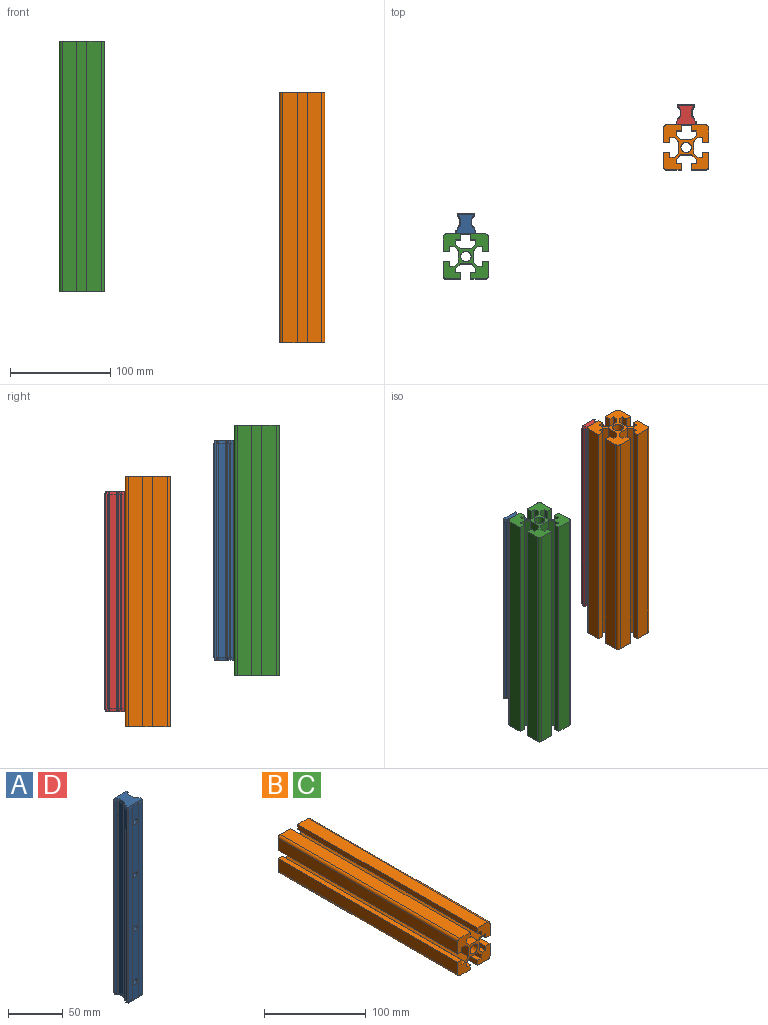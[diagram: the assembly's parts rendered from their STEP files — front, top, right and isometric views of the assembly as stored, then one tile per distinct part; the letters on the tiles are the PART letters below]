
ASSEMBLY  parts=4 mates=2
PART A: 102 faces, bbox 20.1x20.6x220.1 mm
  f0: plane 3.02x1.64mm, normal (0.49,0.85,0.17), area 4mm2, adj f1,f29,f51,f77
  f1: plane 7.51x3mm, normal (0.98,0,0.17), area 21.9mm2, adj f0,f2,f29,f78
  f2: plane 3.04x1.66mm, normal (0.49,-0.85,0.17), area 4mm2, adj f1,f29,f52,f79
  f3: plane 3.07x2.45mm, normal (0.98,0,0.17), area 6.2mm2, adj f29,f50,f51,f75
  f4: plane 3.07x1.9mm, normal (-0.98,0,0.17), area 4.6mm2, adj f29,f35,f36,f57
  f5: plane 3x2.38mm, normal (0.98,0,-0.17), area 6.2mm2, adj f75,f85,f98,f99
  f6: cylinder r=3mm len=12.9mm, axis (0,-1,0), area 243.2mm2, adj f27,f69
  f7: cylinder r=3mm len=12.9mm, axis (0,-1,0), area 243.2mm2, adj f26,f69
  f8: plane 9.4x9.4mm, normal (0,-1,0), area 69.4mm2, adj f19
  f9: plane 3x1.83mm, normal (-0.98,0,-0.17), area 4.6mm2, adj f57,f84,f85,f93
  f10: cone r=2.57mm half-angle=10deg, axis (0,0,-1), area 8mm2, adj f11,f62,f85,f94
  f11: plane 3.04x1.66mm, normal (-0.49,0.85,-0.17), area 4mm2, adj f10,f12,f61,f85
  f12: plane 7.51x3mm, normal (-0.98,0,-0.17), area 21.9mm2, adj f11,f13,f60,f85
  f13: plane 3.02x1.64mm, normal (-0.49,-0.85,-0.17), area 4mm2, adj f12,f59,f85,f93
  f14: plane 9.4x9.4mm, normal (0,-1,0), area 69.4mm2, adj f17
  f15: plane 9.4x9.4mm, normal (0,-1,0), area 69.4mm2, adj f18
  f16: plane 9.4x9.4mm, normal (0,-1,0), area 69.4mm2, adj f20
  f17: cylinder r=4.7mm len=9.4mm, axis (0,-1,0), area 199.3mm2, adj f14,f25
  f18: cylinder r=4.7mm len=9.4mm, axis (0,-1,0), area 199.3mm2, adj f15,f26
  f19: cylinder r=4.7mm len=9.4mm, axis (0,-1,0), area 199.3mm2, adj f8,f27
  f20: cylinder r=4.7mm len=9.4mm, axis (0,-1,0), area 199.3mm2, adj f16,f28
  f21: plane 9.4x9.4mm, normal (0,1,0), area 69.4mm2, adj f31
  f22: plane 9.4x9.4mm, normal (0,1,0), area 69.4mm2, adj f32
  f23: plane 9.4x9.4mm, normal (0,1,0), area 69.4mm2, adj f33
  f24: plane 9.4x9.4mm, normal (0,1,0), area 69.4mm2, adj f34
  f25: plane 9.4x9.4mm, normal (0,1,0), area 41.1mm2, adj f17,f45
  f26: plane 9.4x9.4mm, normal (0,1,0), area 41.1mm2, adj f7,f18
  f27: plane 9.4x9.4mm, normal (0,1,0), area 41.1mm2, adj f6,f19
  f28: plane 9.4x9.4mm, normal (0,1,0), area 41.1mm2, adj f20,f46
  f29: plane 19.49x18.94mm, normal (0,0,1), area 271.6mm2, adj f0,f1,f2,f3,f4,f30,f35,f36
  f30: plane 16.61x3mm, normal (0,0.98,0.17), area 49.9mm2, adj f29,f35,f54,f55
  f31: cylinder r=4.7mm len=9.4mm, axis (0,-1,0), area 3mm2, adj f21,f55
  f32: cylinder r=4.7mm len=9.4mm, axis (0,-1,0), area 3mm2, adj f22,f55
  f33: cylinder r=4.7mm len=9.4mm, axis (0,-1,0), area 3mm2, adj f23,f55
  f34: cylinder r=4.7mm len=9.4mm, axis (0,-1,0), area 3mm2, adj f24,f55
  f35: plane 3x0.71mm, normal (-0.7,0.7,0.17), area 1.5mm2, adj f4,f29,f30,f56
  f36: cone r=2.57mm half-angle=10deg, axis (0,0,1), area 8mm2, adj f4,f29,f37,f58
  f37: plane 3.02x1.64mm, normal (-0.49,-0.85,0.17), area 4mm2, adj f29,f36,f38,f59
  f38: plane 7.51x3mm, normal (-0.98,0,0.17), area 21.9mm2, adj f29,f37,f39,f60
  f39: plane 3.04x1.66mm, normal (-0.49,0.85,0.17), area 4mm2, adj f29,f38,f40,f61
  f40: cone r=2.57mm half-angle=10deg, axis (0,0,1), area 8mm2, adj f29,f39,f41,f62
  f41: plane 3x2.38mm, normal (-0.98,0,0.17), area 6.2mm2, adj f29,f40,f42,f63
  f42: plane 3x1.73mm, normal (-0.49,0.85,0.17), area 4.2mm2, adj f29,f41,f43,f64
  f43: plane 3x2.61mm, normal (-0.98,0,0.17), area 7.1mm2, adj f29,f42,f44,f65
  f44: plane 3x1.42mm, normal (-0.7,-0.7,0.17), area 4.5mm2, adj f29,f43,f47,f66
  f45: cylinder r=3mm len=12.9mm, axis (0,-1,0), area 243.2mm2, adj f25,f69
  f46: cylinder r=3mm len=12.9mm, axis (0,-1,0), area 243.2mm2, adj f28,f69
  f47: plane 17.6x3mm, normal (0,-0.98,0.17), area 39.6mm2, adj f29,f44,f48,f67,f68,f69,f70,f71
  f48: plane 3x1.42mm, normal (0.7,-0.7,0.17), area 4.5mm2, adj f29,f47,f49,f72
  f49: plane 3x2.61mm, normal (0.98,0,0.17), area 7.1mm2, adj f29,f48,f50,f73
  f50: plane 3x1.73mm, normal (0.49,0.85,0.17), area 4.2mm2, adj f3,f29,f49,f74
  f51: cone r=2.57mm half-angle=10deg, axis (0,0,1), area 8mm2, adj f0,f3,f29,f76
  f52: cone r=2.57mm half-angle=10deg, axis (0,0,1), area 8mm2, adj f2,f29,f53,f80
  f53: plane 3x1.83mm, normal (0.98,0,0.17), area 4.6mm2, adj f29,f52,f54,f81
  f54: plane 3x0.71mm, normal (0.7,0.7,0.17), area 1.5mm2, adj f29,f30,f53,f82
  f55: plane 214x16.61mm, normal (0,1,0), area 3277mm2, adj f30,f31,f32,f33,f34,f56,f82,f83
  f56: plane 214x0.5mm, normal (-0.71,0.71,0), area 149.8mm2, adj f35,f55,f57,f84
  f57: plane 214x1.83mm, normal (-1,0,0), area 391.7mm2, adj f4,f9,f56,f58
  f58: cylinder r=2.31mm len=214mm, axis (0,0,-1), area 568.4mm2, adj f36,f57,f59,f93
  f59: plane 214x1.09mm, normal (-0.5,-0.87,0), area 269.8mm2, adj f13,f37,f58,f60
  f60: plane 214x6.9mm, normal (-1,0,0), area 1476.6mm2, adj f12,f38,f59,f61
  f61: plane 214x1.09mm, normal (-0.5,0.87,0), area 269.8mm2, adj f11,f39,f60,f62
  f62: cylinder r=2.31mm len=214mm, axis (0,0,-1), area 568.4mm2, adj f10,f40,f61,f63
  f63: plane 214x2.08mm, normal (-1,0,0), area 444.1mm2, adj f41,f62,f64,f94
  f64: plane 214x1.2mm, normal (-0.5,0.87,0), area 296.5mm2, adj f42,f63,f65,f92
  f65: plane 214x2.61mm, normal (-1,0,0), area 557.9mm2, adj f43,f64,f66,f91
  f66: plane 214x1.2mm, normal (-0.71,-0.71,0), area 363.2mm2, adj f44,f65,f67,f90
  f67: plane 214x4.8mm, normal (0,-1,0), area 1027.2mm2, adj f47,f66,f68,f97
  f68: plane 217.4x0.3mm, normal (0.71,-0.71,0), area 91.5mm2, adj f47,f67,f69,f97
  f69: plane 217.4x7.4mm, normal (0,-1,0), area 1495.7mm2, adj f6,f7,f45,f46,f47,f68,f70,f97
  f70: plane 217.4x0.3mm, normal (-0.71,-0.71,0), area 91.5mm2, adj f47,f69,f71,f97
  f71: plane 214x4.8mm, normal (0,-1,0), area 1027.2mm2, adj f47,f70,f72,f97
  f72: plane 214x1.2mm, normal (0.71,-0.71,0), area 363.2mm2, adj f48,f71,f73,f95
  f73: plane 214x2.61mm, normal (1,0,0), area 557.9mm2, adj f49,f72,f74,f96
  f74: plane 214x1.2mm, normal (0.5,0.87,0), area 296.5mm2, adj f50,f73,f75,f98
  f75: plane 214x2.08mm, normal (1,0,0), area 444.1mm2, adj f3,f5,f74,f76
  f76: cylinder r=2.31mm len=214mm, axis (0,0,-1), area 568.4mm2, adj f51,f75,f77,f99
  f77: plane 214x1.09mm, normal (0.5,0.87,0), area 269.8mm2, adj f0,f76,f78,f89
  f78: plane 214x6.9mm, normal (1,0,0), area 1476.6mm2, adj f1,f77,f79,f88
  f79: plane 214x1.09mm, normal (0.5,-0.87,0), area 269.8mm2, adj f2,f78,f80,f87
  f80: cylinder r=2.31mm len=214mm, axis (0,0,-1), area 568.4mm2, adj f52,f79,f81,f100
  f81: plane 214x1.83mm, normal (1,0,0), area 391.7mm2, adj f53,f80,f82,f101
  f82: plane 214x0.5mm, normal (0.71,0.71,0), area 149.8mm2, adj f54,f55,f81,f86
  f83: plane 16.61x3mm, normal (0,0.98,-0.17), area 49.9mm2, adj f55,f84,f85,f86
  f84: plane 3x0.71mm, normal (-0.7,0.7,-0.17), area 1.5mm2, adj f9,f56,f83,f85
  f85: plane 19.49x18.94mm, normal (0,0,-1), area 271.6mm2, adj f5,f9,f10,f11,f12,f13,f83,f84
  f86: plane 3x0.71mm, normal (0.7,0.7,-0.17), area 1.5mm2, adj f82,f83,f85,f101
  f87: plane 3.04x1.66mm, normal (0.49,-0.85,-0.17), area 4mm2, adj f79,f85,f88,f100
  f88: plane 7.51x3mm, normal (0.98,0,-0.17), area 21.9mm2, adj f78,f85,f87,f89
  f89: plane 3.02x1.64mm, normal (0.49,0.85,-0.17), area 4mm2, adj f77,f85,f88,f99
  f90: plane 3x1.42mm, normal (-0.7,-0.7,-0.17), area 4.5mm2, adj f66,f85,f91,f97
  f91: plane 3x2.61mm, normal (-0.98,0,-0.17), area 7.1mm2, adj f65,f85,f90,f92
  f92: plane 3x1.73mm, normal (-0.49,0.85,-0.17), area 4.2mm2, adj f64,f85,f91,f94
  f93: cone r=2.57mm half-angle=10deg, axis (0,0,-1), area 8mm2, adj f9,f13,f58,f85
  f94: plane 3x2.38mm, normal (-0.98,0,-0.17), area 6.2mm2, adj f10,f63,f85,f92
  f95: plane 3x1.42mm, normal (0.7,-0.7,-0.17), area 4.5mm2, adj f72,f85,f96,f97
  f96: plane 3x2.61mm, normal (0.98,0,-0.17), area 7.1mm2, adj f73,f85,f95,f98
  f97: plane 17.6x3mm, normal (0,-0.98,-0.17), area 39.6mm2, adj f67,f68,f69,f70,f71,f85,f90,f95
  f98: plane 3x1.73mm, normal (0.49,0.85,-0.17), area 4.2mm2, adj f5,f74,f85,f96
  f99: cone r=2.57mm half-angle=10deg, axis (0,0,-1), area 8mm2, adj f5,f76,f85,f89
  f100: cone r=2.57mm half-angle=10deg, axis (0,0,-1), area 8mm2, adj f80,f85,f87,f101
  f101: plane 3x1.83mm, normal (0.98,0,-0.17), area 4.6mm2, adj f81,f85,f86,f100
PART B: 51 faces, bbox 45x250x45 mm
  f0: plane 250x6mm, normal (-1,0,0), area 1500mm2, adj f1,f48,f49,f50
  f1: plane 250x14.5mm, normal (0,0,-1), area 3625mm2, adj f0,f2,f49,f50
  f2: cylinder r=3mm len=250mm, axis (0,-1,0), area 1178.1mm2, adj f1,f3,f49,f50
  f3: plane 250x14.5mm, normal (1,0,0), area 3625mm2, adj f2,f4,f49,f50
  f4: plane 250x6mm, normal (0,0,1), area 1500mm2, adj f3,f5,f49,f50
  f5: plane 250x5mm, normal (-1,0,0), area 1250mm2, adj f4,f6,f49,f50
  f6: plane 250x4.73mm, normal (0,0,1), area 1183.1mm2, adj f5,f7,f49,f50
  f7: plane 250x4.27mm, normal (0.71,0,0.71), area 1508.9mm2, adj f6,f8,f49,f50
  f8: plane 250x11.46mm, normal (1,0,0), area 2866.1mm2, adj f7,f9,f49,f50
  f9: plane 250x4.27mm, normal (0.71,0,-0.71), area 1508.9mm2, adj f8,f10,f49,f50
  f10: plane 250x4.73mm, normal (0,0,-1), area 1183.1mm2, adj f9,f11,f49,f50
  f11: plane 250x5mm, normal (-1,0,0), area 1250mm2, adj f10,f12,f49,f50
  f12: plane 250x6mm, normal (0,0,-1), area 1500mm2, adj f11,f13,f49,f50
  f13: plane 250x14.5mm, normal (1,0,0), area 3625mm2, adj f12,f14,f49,f50
  f14: cylinder r=3mm len=250mm, axis (0,-1,0), area 1178.1mm2, adj f13,f15,f49,f50
  f15: plane 250x14.5mm, normal (0,0,1), area 3625mm2, adj f14,f16,f49,f50
  f16: plane 250x6mm, normal (-1,0,0), area 1500mm2, adj f15,f17,f49,f50
  f17: plane 250x5mm, normal (0,0,-1), area 1250mm2, adj f16,f18,f49,f50
  f18: plane 250x4.73mm, normal (-1,0,0), area 1183.1mm2, adj f17,f19,f49,f50
  f19: plane 250x4.27mm, normal (-0.71,0,0.71), area 1508.9mm2, adj f18,f20,f49,f50
  f20: plane 250x11.46mm, normal (0,0,1), area 2866.1mm2, adj f19,f21,f49,f50
  f21: plane 250x4.27mm, normal (0.71,0,0.71), area 1508.9mm2, adj f20,f22,f49,f50
  f22: plane 250x4.73mm, normal (1,0,0), area 1183.1mm2, adj f21,f23,f49,f50
  f23: plane 250x5mm, normal (0,0,-1), area 1250mm2, adj f22,f24,f49,f50
  f24: plane 250x6mm, normal (1,0,0), area 1500mm2, adj f23,f25,f49,f50
  f25: plane 250x14.5mm, normal (0,0,1), area 3625mm2, adj f24,f26,f49,f50
  f26: cylinder r=3mm len=250mm, axis (0,-1,0), area 1178.1mm2, adj f25,f27,f49,f50
  f27: plane 250x14.5mm, normal (-1,0,0), area 3625mm2, adj f26,f28,f49,f50
  f28: plane 250x6mm, normal (0,0,-1), area 1500mm2, adj f27,f29,f49,f50
  f29: plane 250x5mm, normal (1,0,0), area 1250mm2, adj f28,f30,f49,f50
  f30: plane 250x4.73mm, normal (0,0,-1), area 1183.1mm2, adj f29,f31,f49,f50
  f31: plane 250x4.27mm, normal (-0.71,0,-0.71), area 1508.9mm2, adj f30,f32,f49,f50
  f32: plane 250x11.46mm, normal (-1,0,0), area 2866.1mm2, adj f31,f33,f49,f50
  f33: plane 250x4.27mm, normal (-0.71,0,0.71), area 1508.9mm2, adj f32,f34,f49,f50
  f34: plane 250x4.73mm, normal (0,0,1), area 1183.1mm2, adj f33,f35,f49,f50
  f35: plane 250x5mm, normal (1,0,0), area 1250mm2, adj f34,f36,f49,f50
  f36: plane 250x6mm, normal (0,0,1), area 1500mm2, adj f35,f37,f49,f50
  f37: plane 250x14.5mm, normal (-1,0,0), area 3625mm2, adj f36,f38,f49,f50
  f38: cylinder r=3mm len=250mm, axis (0,-1,0), area 1178.1mm2, adj f37,f39,f49,f50
  f39: plane 250x14.5mm, normal (0,0,-1), area 3625mm2, adj f38,f40,f49,f50
  f40: plane 250x6mm, normal (1,0,0), area 1500mm2, adj f39,f41,f49,f50
  f41: plane 250x5mm, normal (0,0,1), area 1250mm2, adj f40,f42,f49,f50
  f42: plane 250x4.73mm, normal (1,0,0), area 1183.1mm2, adj f41,f43,f49,f50
  f43: plane 250x4.27mm, normal (0.71,0,-0.71), area 1508.9mm2, adj f42,f44,f49,f50
  f44: plane 250x11.46mm, normal (0,0,-1), area 2866.1mm2, adj f43,f45,f49,f50
  f45: plane 250x4.27mm, normal (-0.71,0,-0.71), area 1508.9mm2, adj f44,f46,f49,f50
  f46: plane 250x4.73mm, normal (-1,0,0), area 1183.1mm2, adj f45,f48,f49,f50
  f47: cylinder r=5.25mm len=250mm, axis (0,-1,0), area 8246.7mm2, adj f49,f50
  f48: plane 250x5mm, normal (0,0,1), area 1250mm2, adj f0,f46,f49,f50
  f49: plane 45x45mm, normal (0,1,0), area 1043.5mm2, adj f0,f1,f2,f3,f4,f5,f6,f7
  f50: plane 45x45mm, normal (0,-1,0), area 1043.5mm2, adj f0,f1,f2,f3,f4,f5,f6,f7
PART C: same geometry as B
PART D: same geometry as A
PLACE A t=(-220.27,-109.14,51.35)mm
PLACE B rot(axis=(-1,0,0),90deg) t=(0,-22.2,15)mm
PLACE C rot(axis=(1,0,0),90deg) t=(-220.27,-131.34,-183.65)mm
PLACE D at identity
MATE fastened B.f15 <-> D.f69  axis (0,1,0) through (0,0.3,-110)mm
MATE fastened C.f1 <-> A.f69  axis (0,1,0) through (-220.27,-108.84,-58.65)mm
